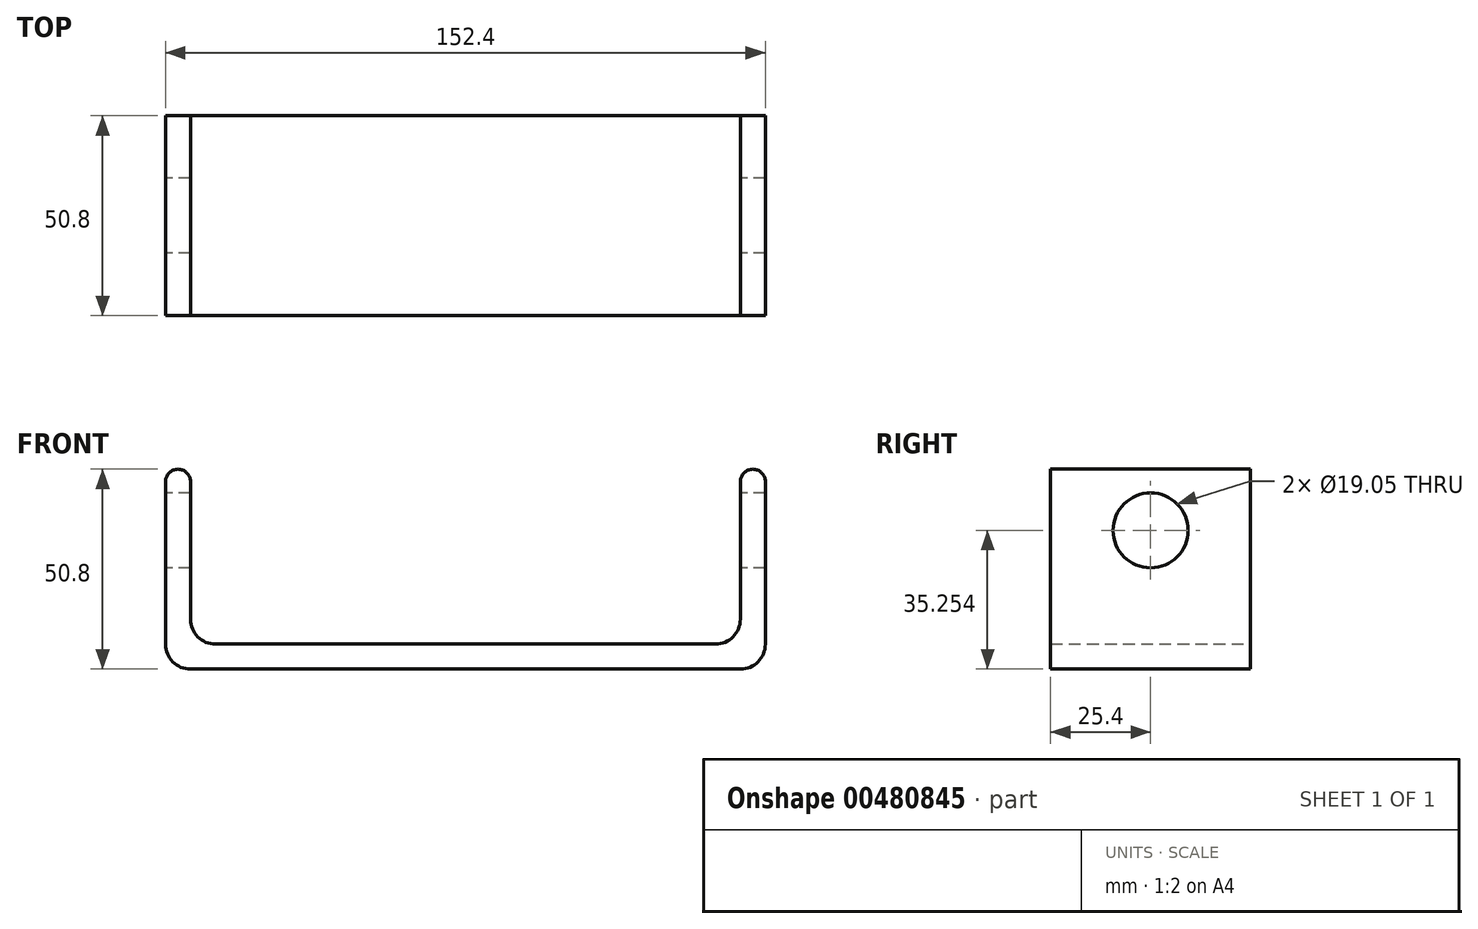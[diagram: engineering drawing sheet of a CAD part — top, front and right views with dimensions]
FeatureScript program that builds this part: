
annotation { "Feature Type Name" : "Feature", "Feature Type Description" : "" }
export const myFeature = defineFeature(function(context is Context, id is Id, definition is map)
    precondition{}
    {
        {
            var Q0;
            Q0=qCreatedBy(makeId("Front.planeOp"),FACE);
            var sketch = newSketch(context, id + "F0", { "sketchPlane" : qUnion([Q0])});
            skLineSegment(sketch, "E0", {"start": v(0, 0) * mm, "end": v(76.2, 0) * mm});
            skLineSegment(sketch, "E1", {"start": v(76.2, 0) * mm, "end": v(76.2, 50.8) * mm});
            skLineSegment(sketch, "E2.0", {"start": v(69.85, 6.35) * mm, "end": v(69.85, 50.8) * mm});
            skLineSegment(sketch, "E2.1", {"start": v(0, 6.35) * mm, "end": v(69.85, 6.35) * mm});
            skLineSegment(sketch, "E3", {"start": v(69.85, 50.8) * mm, "end": v(76.2, 50.8) * mm});
            skLineSegment(sketch, "E4.MirrorCS", {"start": v(-69.85, 6.35) * mm, "end": v(-69.85, 50.8) * mm});
            skLineSegment(sketch, "E5.MirrorCS", {"start": v(-69.85, 50.8) * mm, "end": v(-76.2, 50.8) * mm});
            skLineSegment(sketch, "E6.MirrorCS", {"start": v(0, 0) * mm, "end": v(-76.2, 0) * mm});
            skLineSegment(sketch, "E7.MirrorCS", {"start": v(0, 6.35) * mm, "end": v(-69.85, 6.35) * mm});
            skLineSegment(sketch, "E8.MirrorCS", {"start": v(-76.2, 0) * mm, "end": v(-76.2, 50.8) * mm});
            skSolve(sketch);
        }
        {
            var Q0;
            Q0 = qSketchRegion(id + "F0", true);
            extrude(context, id + "F1", {"entities" : qUnion([Q0]), "endBound" : BoundingType.SYMMETRIC, "depth" : 50.8 * mm});
        }
        {
            var Q0;
            Q0=makeQuery(id+"F1.opExtrude","SWEPT_EDGE",EDGE,{"disambiguationData":[OSD([sQuery(id+"F0.wireOp",EDGE,"E4.MirrorCS"),sQuery(id+"F0.wireOp",EDGE,"E7.MirrorCS")])]});
            var Q1;
            Q1=makeQuery(id+"F1.opExtrude","SWEPT_EDGE",EDGE,{"disambiguationData":[OSD([sQuery(id+"F0.wireOp",EDGE,"E2.0"),sQuery(id+"F0.wireOp",EDGE,"E2.1")])]});
            var Q2;
            Q2=makeQuery(id+"F1.opExtrude","SWEPT_EDGE",EDGE,{"disambiguationData":[OSD([sQuery(id+"F0.wireOp",EDGE,"E0"),sQuery(id+"F0.wireOp",EDGE,"E1")])]});
            var Q3;
            Q3=makeQuery(id+"F1.opExtrude","SWEPT_EDGE",EDGE,{"disambiguationData":[OSD([sQuery(id+"F0.wireOp",EDGE,"E6.MirrorCS"),sQuery(id+"F0.wireOp",EDGE,"E8.MirrorCS")])]});
            fillet(context, id + "F2", {"entities" : qUnion([Q0, Q1, Q2, Q3]), "radius" : 6.35 * mm, "tangentPropagation" : true, "allowEdgeOverflow" : false});
        }
        {
            var Q0;
            Q0=makeQuery(id+"F1.opExtrude","SWEPT_EDGE",EDGE,{"disambiguationData":[OSD([sQuery(id+"F0.wireOp",EDGE,"E4.MirrorCS"),sQuery(id+"F0.wireOp",EDGE,"E5.MirrorCS")])]});
            var Q1;
            Q1=makeQuery(id+"F1.opExtrude","SWEPT_EDGE",EDGE,{"disambiguationData":[OSD([sQuery(id+"F0.wireOp",EDGE,"E5.MirrorCS"),sQuery(id+"F0.wireOp",EDGE,"E8.MirrorCS")])]});
            var Q2;
            Q2=makeQuery(id+"F1.opExtrude","SWEPT_EDGE",EDGE,{"disambiguationData":[OSD([sQuery(id+"F0.wireOp",EDGE,"E2.0"),sQuery(id+"F0.wireOp",EDGE,"E3")])]});
            var Q3;
            Q3=makeQuery(id+"F1.opExtrude","SWEPT_EDGE",EDGE,{"disambiguationData":[OSD([sQuery(id+"F0.wireOp",EDGE,"E1"),sQuery(id+"F0.wireOp",EDGE,"E3")])]});
            fillet(context, id + "F3", {"entities" : qUnion([Q0, Q1, Q2, Q3]), "radius" : 3.17 * mm, "tangentPropagation" : true, "allowEdgeOverflow" : false});
        }
        {
            var Q0;
            Q0=makeQuery(id+"F1.opExtrude","SWEPT_FACE",FACE,{"disambiguationData":[OSD([sQuery(id+"F0.wireOp",EDGE,"E8.MirrorCS")])]});
            var sketch = newSketch(context, id + "F4", { "sketchPlane" : qUnion([Q0])});
            skLineSegment(sketch, "E9.0", {"start": v(25.4, 47.62) * mm, "end": v(-25.4, 47.62) * mm});
            skLineSegment(sketch, "E10.0", {"start": v(-25.4, 6.35) * mm, "end": v(-25.4, 47.62) * mm});
            skLineSegment(sketch, "E11.0", {"start": v(-25.4, 6.35) * mm, "end": v(25.4, 6.35) * mm});
            skPoint(sketch, "E12.0", {"position": v(25.4, 26.99) * mm});
            skLineSegment(sketch, "E13.0", {"start": v(25.4, 6.35) * mm, "end": v(25.4, 47.62) * mm});
            skCircle(sketch, "E14", {"center": v(0, 35.25) * mm, "radius": 9.53 * mm});
            skPoint(sketch, "E14.centerSnap0", {"position": v(0, 47.62) * mm});
            skSolve(sketch);
        }
        {
            var Q0;
            Q0=makeQuery(id+"F4.imprint","IMPRINT",FACE,{"disambiguationData":[TD([[makeQuery(id+"F4.imprint","IMPRINT",EDGE,{"derivedFrom":sQuery(id+"F4.wireOp",EDGE,"E14")}),1.0]])]});
            extrude(context, id + "F5", {"entities" : qUnion([Q0]), "operationType" : NewBodyOperationType.REMOVE, "endBound" : BoundingType.THROUGH_ALL, "oppositeDirection" : true, "depth" : 25.4 * mm});
        }
    });
